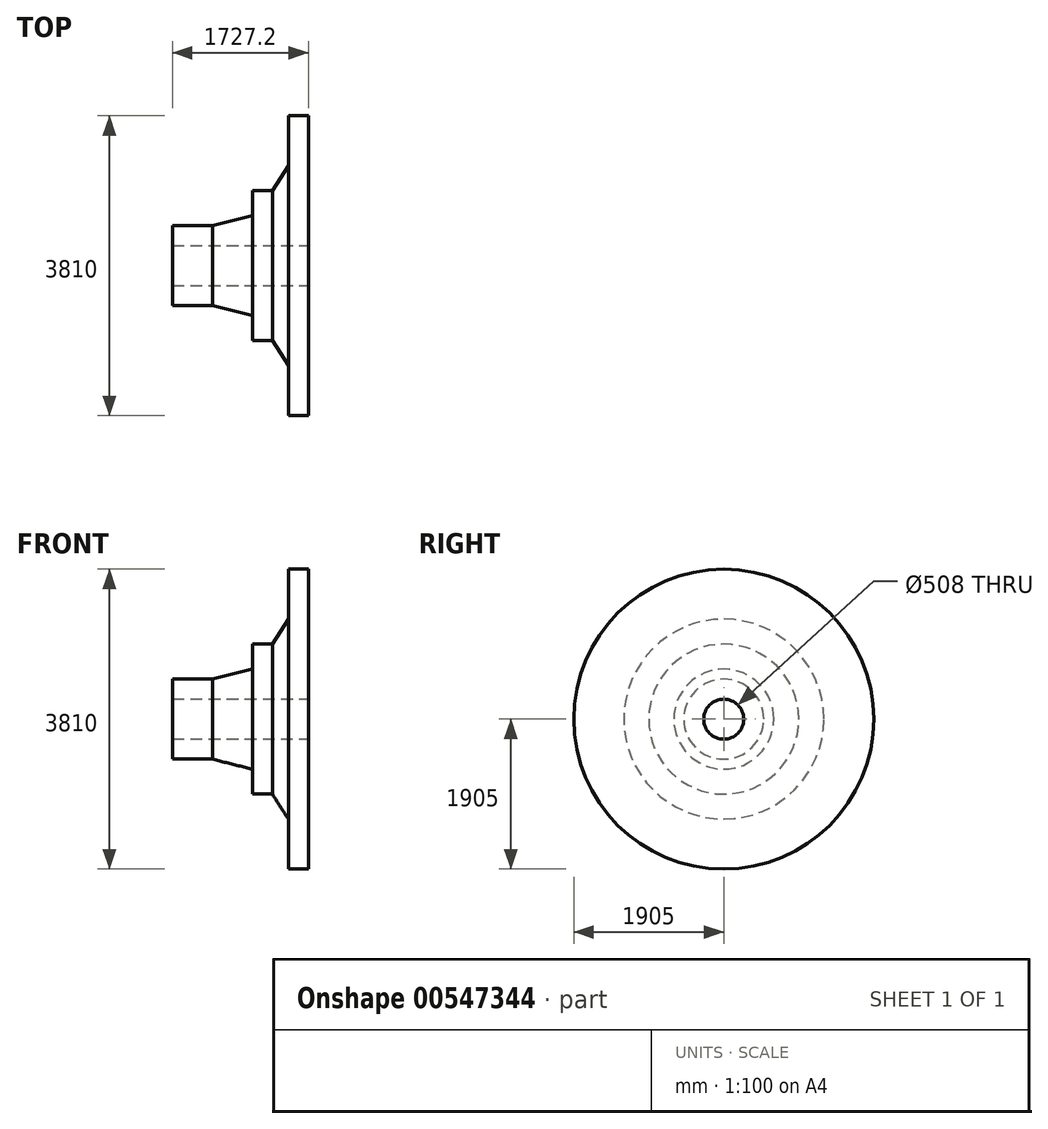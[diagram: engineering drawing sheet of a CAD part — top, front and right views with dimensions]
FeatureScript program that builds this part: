
annotation { "Feature Type Name" : "Feature", "Feature Type Description" : "" }
export const myFeature = defineFeature(function(context is Context, id is Id, definition is map)
    precondition{}
    {
        {
            var Q0;
            Q0=qCreatedBy(makeId("Front.planeOp"),FACE);
            var sketch = newSketch(context, id + "F0", { "sketchPlane" : qUnion([Q0])});
            skLineSegment(sketch, "E0", {"start": v(1844.87, 0) * mm, "end": v(-1873.25, 0) * mm});
            skLineSegment(sketch, "E1", {"start": v(1771.18, 254) * mm, "end": v(43.98, 254) * mm});
            skLineSegment(sketch, "E2", {"start": v(1771.18, 254) * mm, "end": v(1771.18, 1905) * mm});
            skLineSegment(sketch, "E3", {"start": v(1771.18, 1905) * mm, "end": v(1517.18, 1905) * mm});
            skLineSegment(sketch, "E4", {"start": v(1517.18, 1905) * mm, "end": v(1517.18, 1270) * mm});
            skLineSegment(sketch, "E5", {"start": v(1517.18, 1270) * mm, "end": v(1313.98, 952.5) * mm});
            skLineSegment(sketch, "E6", {"start": v(1313.98, 952.5) * mm, "end": v(1059.98, 952.5) * mm});
            skLineSegment(sketch, "E7", {"start": v(1059.98, 952.5) * mm, "end": v(1059.98, 635) * mm});
            skLineSegment(sketch, "E8", {"start": v(1059.98, 635) * mm, "end": v(551.98, 508) * mm});
            skLineSegment(sketch, "E9", {"start": v(551.98, 508) * mm, "end": v(43.98, 508) * mm});
            skLineSegment(sketch, "E10", {"start": v(43.98, 508) * mm, "end": v(43.98, 254) * mm});
            skSolve(sketch);
        }
        {
            var Q0;
            Q0=qSketchRegion(id+"F0",true);
            var Q1;
            Q1=sQuery(id+"F0.wireOp",EDGE,"E0");
            revolve(context, id + "F1", {"entities" : qUnion([Q0]), "axis" : qUnion([Q1]), "revolveType" : RevolveType.FULL});
        }
    });
